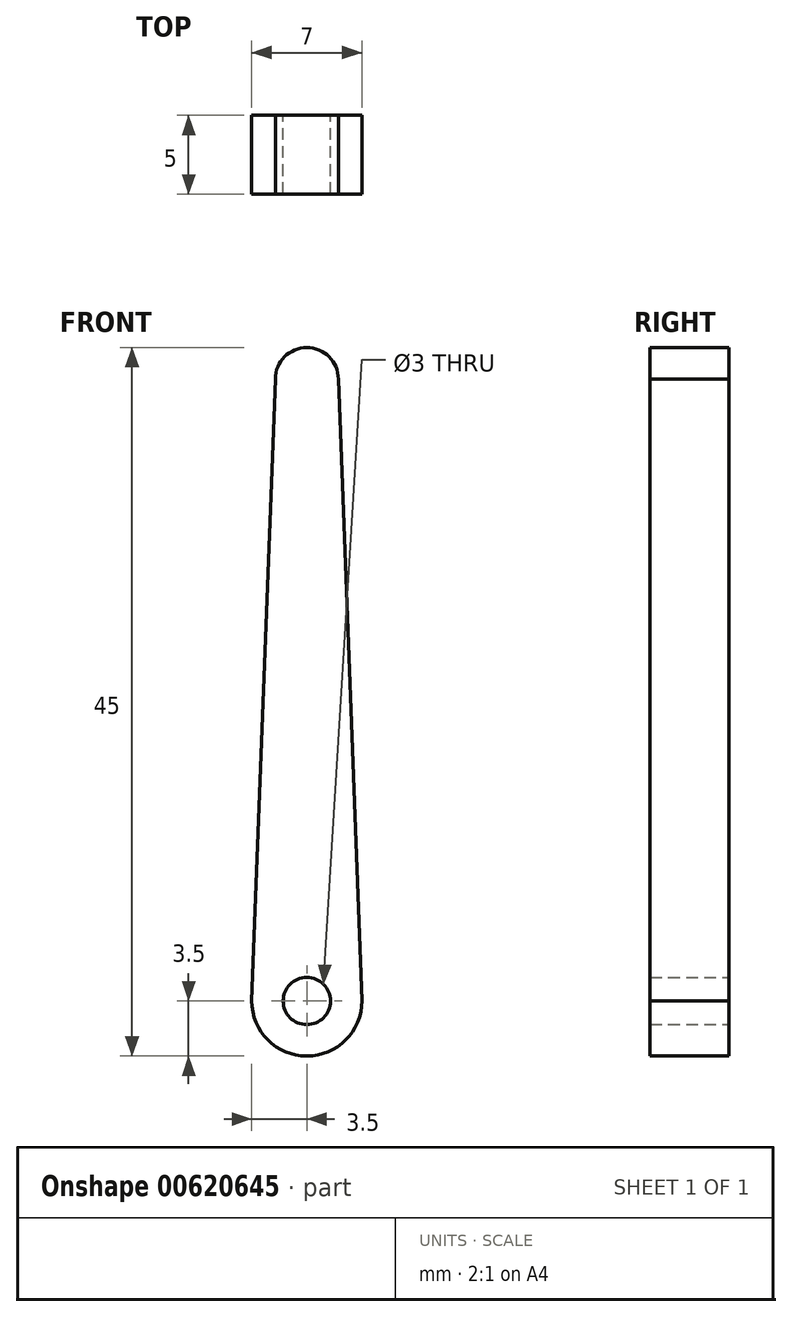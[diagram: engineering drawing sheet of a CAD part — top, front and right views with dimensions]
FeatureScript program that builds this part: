
annotation { "Feature Type Name" : "Feature", "Feature Type Description" : "" }
export const myFeature = defineFeature(function(context is Context, id is Id, definition is map)
    precondition{}
    {
        {
            var Q0;
            Q0=qCreatedBy(makeId("Front.planeOp"),FACE);
            var sketch = newSketch(context, id + "F0", { "sketchPlane" : qUnion([Q0])});
            skCircle(sketch, "E0", {"center": v(0, 0) * mm, "radius": 1.5 * mm});
            skLineSegment(sketch, "E1", {"start": v(-3.5, 0) * mm, "end": v(-2, 39.5) * mm});
            skArc(sketch, "E2", {"start": v(-3.5, 0) * mm, "mid": v(-2.47, -2.47) * mm, "end": v(0, -3.5) * mm});
            skArc(sketch, "E3", {"start": v(-2, 39.5) * mm, "mid": v(-1.41, 40.91) * mm, "end": v(0, 41.5) * mm});
            skArc(sketch, "E4.MirrorCS", {"start": v(2, 39.5) * mm, "mid": v(1.41, 40.91) * mm, "end": v(0, 41.5) * mm});
            skLineSegment(sketch, "E5.MirrorCS", {"start": v(3.5, 0) * mm, "end": v(2, 39.5) * mm});
            skArc(sketch, "E6.MirrorCS", {"start": v(3.5, 0) * mm, "mid": v(2.47, -2.47) * mm, "end": v(0, -3.5) * mm});
            skSolve(sketch);
        }
        {
            var Q0;
            Q0=makeQuery(id+"F0.imprint","IMPRINT",FACE,{"disambiguationData":[TD([[makeQuery(id+"F0.imprint","IMPRINT",EDGE,{"derivedFrom":sQuery(id+"F0.wireOp",EDGE,"E0")}),-1.0]])]});
            extrude(context, id + "F1", {"entities" : qUnion([Q0]), "depth" : 5 * mm, "offsetDistance" : 25 * mm});
        }
    });
